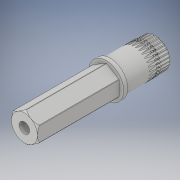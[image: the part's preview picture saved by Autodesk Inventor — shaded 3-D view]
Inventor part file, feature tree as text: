
AUTODESK INVENTOR PART (.ipt)
format: ipt  version: 2017 (Build 210142000, 142)  size: 1,403,392 bytes
history: native  units: in
note: dims shown in document units (in); Inventor stores cm internally (conversion verified against a paired STEP export)
features: fillet x1
ambient origin geometry x8: Origin, YZ Plane, XZ Plane, XY Plane, X Axis, Y Axis, Z Axis, Center Point
bodies: Solid1 (feature_tree)
feature tree (1):
  fillet  "Fillet5"  [1 undecoded]
note: 1 required parameter value undecoded (feature->parameter linkage not recoverable at this tier; creation-order binding heuristic only, values carry confidence <= 0.55)
